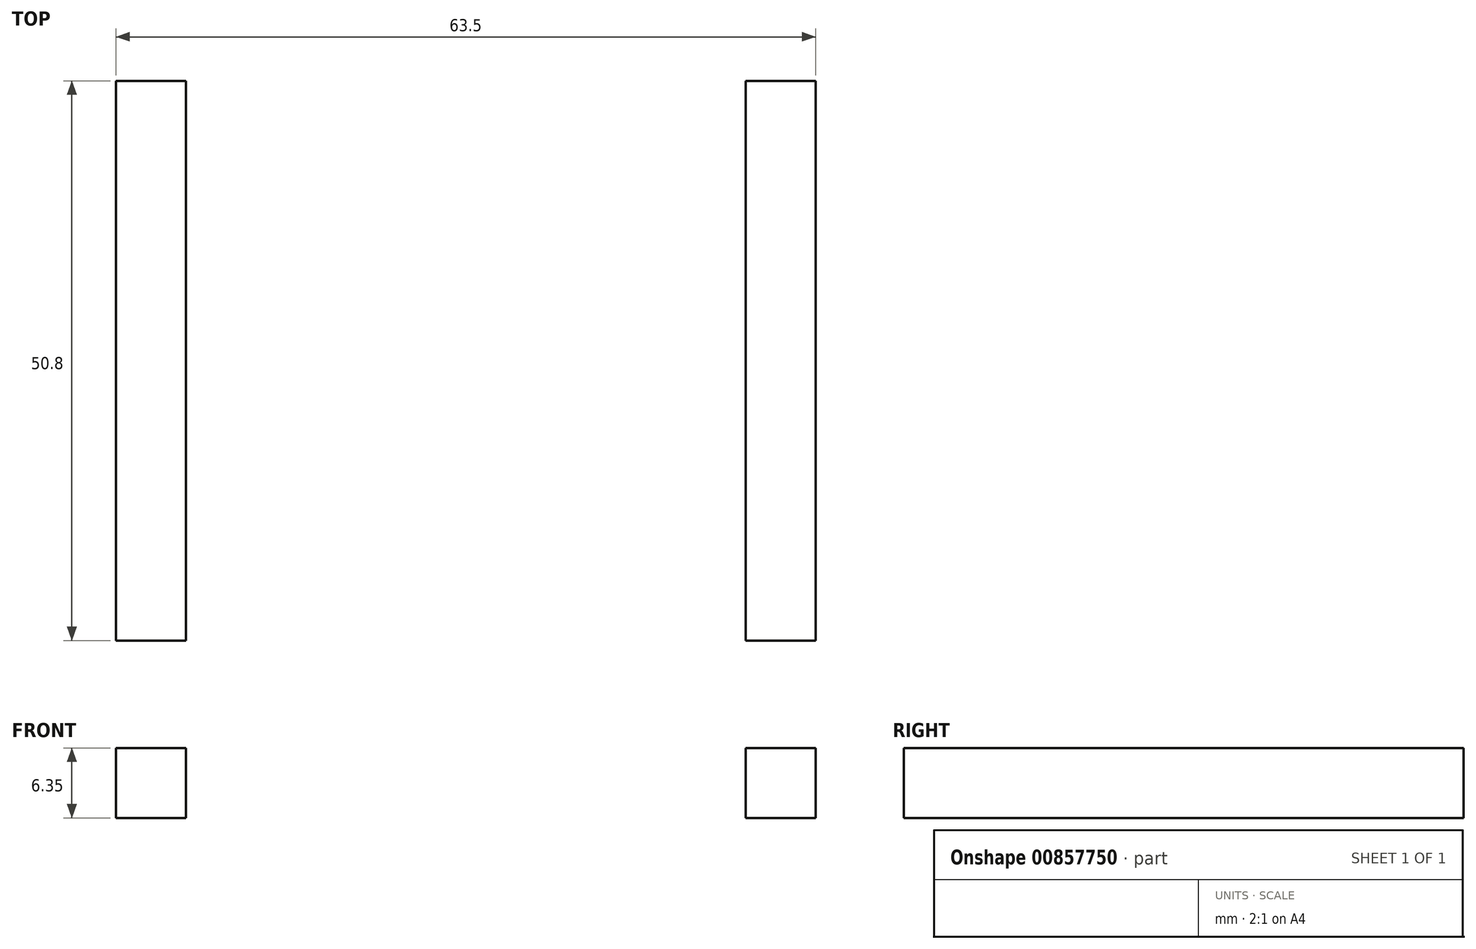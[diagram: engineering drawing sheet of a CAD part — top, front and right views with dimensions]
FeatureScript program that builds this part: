
annotation { "Feature Type Name" : "Feature", "Feature Type Description" : "" }
export const myFeature = defineFeature(function(context is Context, id is Id, definition is map)
    precondition{}
    {
        {
            var Q0;
            Q0=qCreatedBy(makeId("Top.planeOp"),FACE);
            var sketch = newSketch(context, id + "F0", { "sketchPlane" : qUnion([Q0])});
            skLineSegment(sketch, "E0", {"start": v(0, 0) * mm, "end": v(50.8, 0) * mm});
            skLineSegment(sketch, "E1.bottom", {"start": v(0, 0) * mm, "end": v(-6.35, 0) * mm});
            skLineSegment(sketch, "E1.top", {"start": v(0, -50.8) * mm, "end": v(-6.35, -50.8) * mm});
            skLineSegment(sketch, "E1.left", {"start": v(0, 0) * mm, "end": v(0, -50.8) * mm});
            skLineSegment(sketch, "E1.right", {"start": v(-6.35, 0) * mm, "end": v(-6.35, -50.8) * mm});
            skLineSegment(sketch, "E2.bottom", {"start": v(50.8, 0) * mm, "end": v(57.15, 0) * mm});
            skLineSegment(sketch, "E2.top", {"start": v(50.8, -50.8) * mm, "end": v(57.15, -50.8) * mm});
            skLineSegment(sketch, "E2.left", {"start": v(50.8, 0) * mm, "end": v(50.8, -50.8) * mm});
            skLineSegment(sketch, "E2.right", {"start": v(57.15, 0) * mm, "end": v(57.15, -50.8) * mm});
            skSolve(sketch);
        }
        {
            var Q0;
            Q0 = qSketchRegion(id + "F0", true);
            extrude(context, id + "F1", {"entities" : qUnion([Q0]), "depth" : 6.35 * mm, "offsetDistance" : 25.4 * mm});
        }
    });
